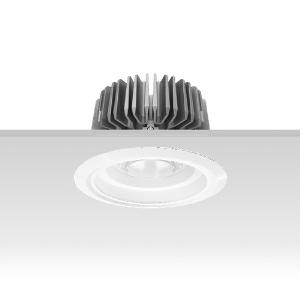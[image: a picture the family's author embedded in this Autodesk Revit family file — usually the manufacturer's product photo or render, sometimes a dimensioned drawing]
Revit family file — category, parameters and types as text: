
# Revit family: 3f_filippi_-_3f_reno_bianco_ampio_3f_filippi_-_30345_a01023_-_3f_reno_150_wh_2000-930_wide___vt_wh_422c
name_source: partatom
category: Lighting Fixtures
units: mm (PartAtom-declared; Revit-internal decimal feet)

## family parameters
Cut with Voids When Loaded = No
Host = Face
Light Source = No
Part Type = Normal
Room Calculation Point = No
Round Connector Dimension = Use Diameter
Shared = No

## types (1)
- 3F Filippi - 3F Reno Bianco Ampio (1 x LED, 1888 lm, 24 W, 3000 K)
    Apparent Load = 24 VA
    Approval mark = CE
    CIE Flux Codes = 74 93 99 100 100
    Color Rendering = 90
    Color Temperature = 3000 K
    Control Gear = Electronic ballast
    Default Elevation = 1800 mm
    Description = ILLUMINOTECHNICAL
Luminous efficiency 100% (DLOR 100%, ULOR 0%).
Initial luminous flux of the luminaire 1888 lm.
Direct symmetric wide distribution.
Installation Interdistance Transv.D = 1.54 x hu - Long.D = 1.54 x hu.
Tabular UGR (CIE 117 - 4H-8H; S=0.25H; 70/50/20): RUG 23.2 - 23.
Beam angle: 74° - 73°.
Luminous efficacy 79 lm/W.
Lifetime (L90/B10): 30000 h. (tq+25°C)
Lifetime (L85/B10): 50000 h. (tq+25°C)
Lifetime (L70/B10): 80000 h. (tq+25°C)
Sudden decreased luminous flux after 50000 hours: 0% (C0).
Photobiological safety in compliance with IEC/TR 62778: RG0 risk exempt, (IEC 62471).
In compliance with IEC/EN 62722-2-1 - IEC/EN 62717 standards.

SOURCE
Compact LED module 2000/930.
Energy efficiency class (UE 2019/2020 - UE 2019/2015): E.
CIE 13.3 Colour rendering index: CRI >90 (R9 >50%).
IES TM-30 Fidelity Index: Rf = 92 Rg = 101.
CCT nominal colour temperature 3000 K.
Colour initial tolerance (MacAdam): SDCM 3.
Zhaga Book 3 compliant.

MECHANICAL
Passive heat dissipator in die-casting aluminium, oversized, for optimum thermal management of the LED module.
Parabolic element with graduated/concentric rings in white polycarbonate.
Transparent external lens with glossy and satin differentiated surfaces, with a cooling and anti-insect system in methacrylate (PMMA).
Fastening spring clips in stainless steel.
Dimensions: diameter 176 mm, height 111 mm. Weight 0.81 kg.
IP44 protection degree for exposed part, IP20 for recessed part.
Mechanical strength to impacts IK06 (1 joule).
Glow-wire test resistance 650°C.

ELECTRICAL
Wiring on a separate unit.
Halogen Free electronic wiring 230V-50/60Hz, power factor 0.95, THD <25%, constant output current, SELV, class II, 1 driver.
Power of the luminaire 24 W.
ENEC - CE.
SAFE FLICKER: PstLM=<1 and SVM=<0.4 (IEC TR 61547-1 and IEC TR 63158), to ensure a more comfortable and safe light.
Luminaire compliant with EN 60598-2-22 for power supply from a centralised emergency system CPSS (Central Power Supply System), not incorporated in the luminaire - high risk areas excluded. The default power and flux are 100% in AC and 100% in DC.
Ambient temperature from 0°C to +25°C.
Temperature class T6 max 85°C.
Relative humidity UR: <85%.

INSTALLATION
Pull-up recessed fitting.
False ceiling carving: 150 mm.
All accessories dedicated to this product are available on the Catalog and on our website www.3F-Filippi.com.

ACCESSORIES
A01023 - VT transparent glass, tempered, not flammable, locked and in line with the trim, in white polycarbonate.

APPLICATIONS
Environments: architectural, commercial, exhibition areas, transit areas, corridors, shops, display windows, service areas.
In false ceilings with narrow voids.

WARNING
Luminaire designed for disposal/recycling at end-of-life.
Replaceable (LED only) light source by a professional. Replaceable control gear by a professional.
    Height = 0 mm  [stored 0 ft]
    Lamp = 1 x LED
    Lamp Light Flux = 1888 lm
    Lamp Power = 24 W
    Lamp count = 1
    Length = 176 mm
    Lifetime = 50000 h
    Luminous efficacy = 79 lm/W
    Manufacturer = 3F Filippi
    ModVariant = No
    Model = 3F Filippi - 30345+A01023 - 3F Reno 150 WH 2000-930 WIDE + VT WH
    Mounting Place = Ceiling
    Mounting Type = Recessed
    Number of Poles = 1
    OnlyDefault = Yes
    Power Factor = 1
    Product Name = 3F Filippi - 3F Reno Bianco Ampio
    Product group = recessed luminaire
    ProductGroupID = 4
    Protection Class = Protection class II
    Protection Degree = IP 20
    RLX_Detail_Level = 1
    RLX_Emergency_Light_Flux = 0 lm
    RLX_Emergency_Type = 0
    RLX_Emergency_Type_DB = No
    RlxData = <blob elided: 84849 chars, md5=9ace0583>
    Socket = socket
    Standby Power = 0 W
    System Light Flux = 1888 lm
    System Power = 24 W
    Type Comments = Product without accessories
    Type Image = 3ffilippi_3f_reno_150_wh_d150__a01023.jpg
    URL = http://relux.com
    VarID = ---
    Voltage = 0 V
    Weight = 0.00 kg
    Width = 0 mm  [stored 0 ft]

note: [stored X ft] marks values corroborated as IEEE doubles in the binary element streams (Revit-internal decimal feet)

## geometry (parser evidence)
native form markers: Blend x4, Sweep x11
no freeform markers — native parametric forms only
